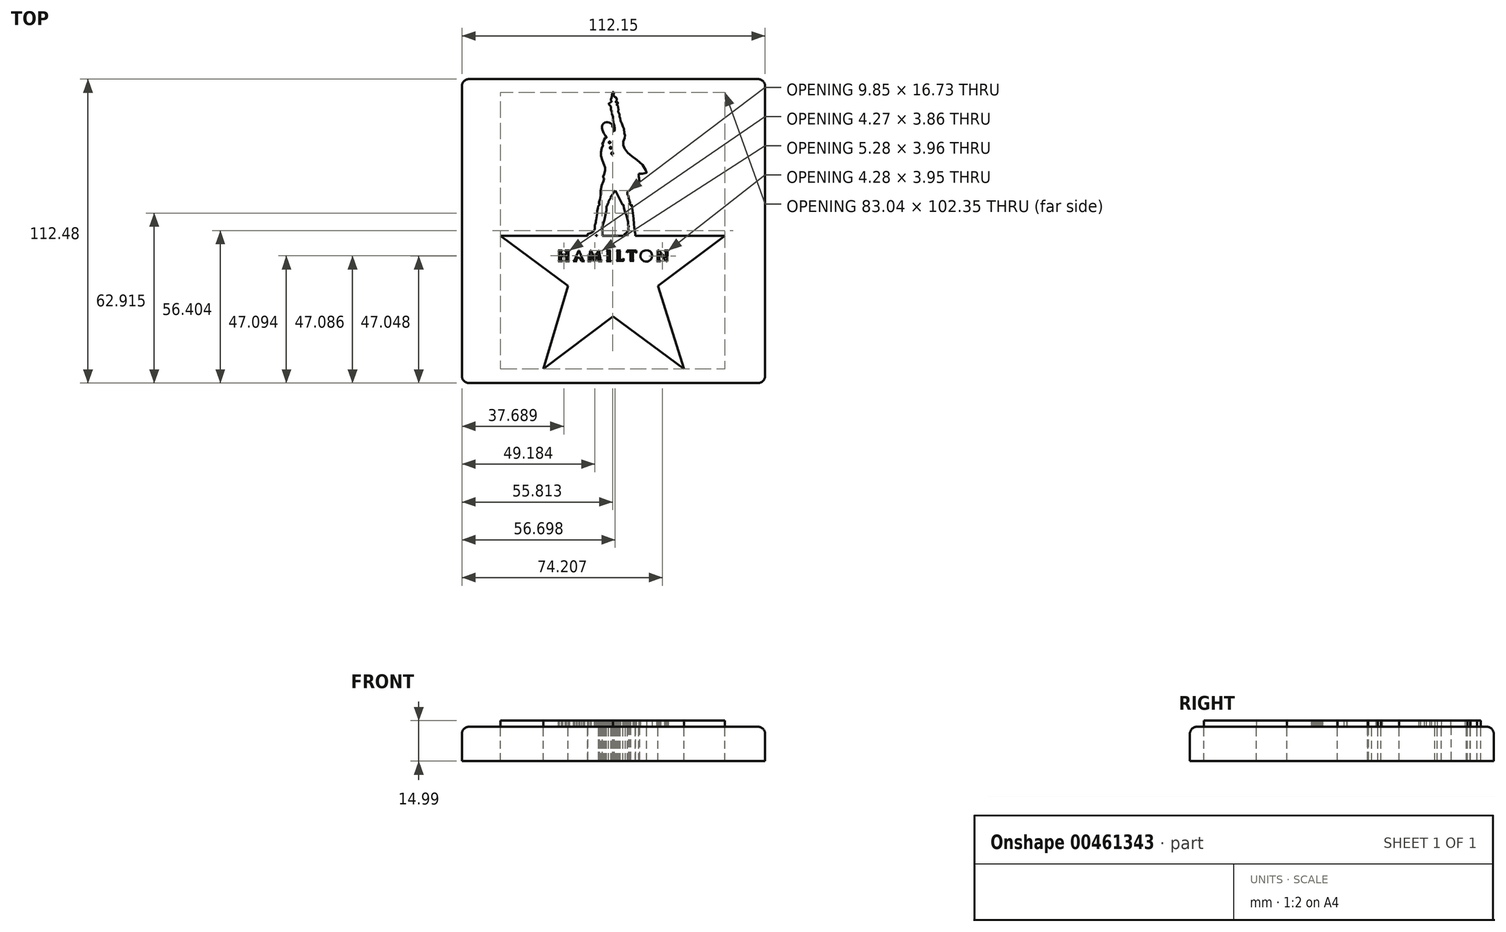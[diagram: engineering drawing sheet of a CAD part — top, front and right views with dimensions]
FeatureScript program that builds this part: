
annotation { "Feature Type Name" : "Feature", "Feature Type Description" : "" }
export const myFeature = defineFeature(function(context is Context, id is Id, definition is map)
    precondition{}
    {
        {
            var Q0;
            Q0=qCreatedBy(makeId("Top.planeOp"),FACE);
            var sketch = newSketch(context, id + "F0", { "sketchPlane" : qUnion([Q0])});
            skLineSegment(sketch, "E0.bottom", {"start": v(-76.02, 56.24) * mm, "end": v(36.13, 56.24) * mm});
            skLineSegment(sketch, "E0.top", {"start": v(-76.02, -56.24) * mm, "end": v(36.13, -56.24) * mm});
            skLineSegment(sketch, "E0.left", {"start": v(-76.02, 56.24) * mm, "end": v(-76.02, -56.24) * mm});
            skLineSegment(sketch, "E0.right", {"start": v(36.13, 56.24) * mm, "end": v(36.13, -56.24) * mm});
            skLineSegment(sketch, "E1", {"start": v(-61.73, -1.69) * mm, "end": v(21.31, -1.69) * mm});
            skLineSegment(sketch, "E2", {"start": v(21.31, -1.69) * mm, "end": v(-3.46, -20.29) * mm});
            skLineSegment(sketch, "E3", {"start": v(-3.46, -20.29) * mm, "end": v(6.1, -51.01) * mm});
            skLineSegment(sketch, "E4", {"start": v(6.1, -51.01) * mm, "end": v(-20.13, -31.64) * mm});
            skLineSegment(sketch, "E5", {"start": v(-20.13, -31.64) * mm, "end": v(-45.97, -51.01) * mm});
            skLineSegment(sketch, "E6", {"start": v(-45.97, -51.01) * mm, "end": v(-36.74, -20.29) * mm});
            skLineSegment(sketch, "E7", {"start": v(-36.74, -20.29) * mm, "end": v(-61.73, -1.69) * mm});
            skLineSegment(sketch, "E8", {"start": v(-40.47, -7.22) * mm, "end": v(-38.99, -7.22) * mm});
            skLineSegment(sketch, "E9", {"start": v(-38.99, -7.22) * mm, "end": v(-39.25, -7.42) * mm});
            skLineSegment(sketch, "E10", {"start": v(-39.25, -7.42) * mm, "end": v(-39.25, -8.79) * mm});
            skLineSegment(sketch, "E11", {"start": v(-39.25, -8.79) * mm, "end": v(-37.42, -8.79) * mm});
            skLineSegment(sketch, "E12", {"start": v(-40.47, -7.22) * mm, "end": v(-40.03, -7.54) * mm});
            skLineSegment(sketch, "E13", {"start": v(-40.03, -7.54) * mm, "end": v(-40.03, -10.72) * mm});
            skLineSegment(sketch, "E14", {"start": v(-40.03, -10.72) * mm, "end": v(-40.47, -11.08) * mm});
            skLineSegment(sketch, "E15", {"start": v(-40.47, -11.08) * mm, "end": v(-38.8, -11.08) * mm});
            skLineSegment(sketch, "E16", {"start": v(-39.25, -9.22) * mm, "end": v(-37.46, -9.22) * mm});
            skLineSegment(sketch, "E17", {"start": v(-37.46, -9.22) * mm, "end": v(-37.46, -10.72) * mm});
            skPoint(sketch, "E18.start.orphan", {"position": v(-39.18, -10.72) * mm});
            skLineSegment(sketch, "E19", {"start": v(-39.25, -9.22) * mm, "end": v(-39.25, -10.73) * mm});
            skLineSegment(sketch, "E20", {"start": v(-39.25, -10.73) * mm, "end": v(-38.8, -11.08) * mm});
            skLineSegment(sketch, "E21", {"start": v(-37.46, -10.72) * mm, "end": v(-37.82, -11.08) * mm});
            skLineSegment(sketch, "E22", {"start": v(-37.82, -11.08) * mm, "end": v(-36.2, -11.08) * mm});
            skLineSegment(sketch, "E23", {"start": v(-36.2, -11.08) * mm, "end": v(-36.62, -10.72) * mm});
            skLineSegment(sketch, "E24", {"start": v(-36.62, -10.72) * mm, "end": v(-36.62, -7.61) * mm});
            skPoint(sketch, "E25.end.orphan", {"position": v(-36.2, -7.32) * mm});
            skLineSegment(sketch, "E26", {"start": v(-37.42, -8.79) * mm, "end": v(-37.42, -7.54) * mm});
            skLineSegment(sketch, "E27", {"start": v(-37.42, -7.54) * mm, "end": v(-37.88, -7.22) * mm});
            skLineSegment(sketch, "E28", {"start": v(-37.88, -7.22) * mm, "end": v(-36.23, -7.22) * mm});
            skLineSegment(sketch, "E29", {"start": v(-36.23, -7.22) * mm, "end": v(-36.62, -7.61) * mm});
            skLineSegment(sketch, "E30", {"start": v(-32.93, -8.38) * mm, "end": v(-33.3, -9.34) * mm});
            skLineSegment(sketch, "E31", {"start": v(-33.3, -9.34) * mm, "end": v(-32.52, -9.34) * mm});
            skLineSegment(sketch, "E32", {"start": v(-32.52, -9.34) * mm, "end": v(-32.93, -8.38) * mm});
            skLineSegment(sketch, "E33", {"start": v(-33.5, -11.1) * mm, "end": v(-34.91, -11.1) * mm});
            skLineSegment(sketch, "E34", {"start": v(-34.91, -11.1) * mm, "end": v(-34.4, -10.75) * mm});
            skLineSegment(sketch, "E35", {"start": v(-34.4, -10.75) * mm, "end": v(-32.86, -7.19) * mm});
            skLineSegment(sketch, "E36", {"start": v(-32.86, -7.19) * mm, "end": v(-32.7, -7.19) * mm});
            skLineSegment(sketch, "E37", {"start": v(-32.7, -7.19) * mm, "end": v(-31.12, -10.83) * mm});
            skLineSegment(sketch, "E38", {"start": v(-33.5, -9.83) * mm, "end": v(-32.43, -9.83) * mm});
            skLineSegment(sketch, "E39", {"start": v(-32.43, -9.83) * mm, "end": v(-31.86, -11.1) * mm});
            skLineSegment(sketch, "E40", {"start": v(-31.86, -11.1) * mm, "end": v(-30.73, -11.1) * mm});
            skLineSegment(sketch, "E41", {"start": v(-30.73, -11.1) * mm, "end": v(-31.12, -10.83) * mm});
            skLineSegment(sketch, "E42", {"start": v(-33.5, -9.83) * mm, "end": v(-33.78, -10.76) * mm});
            skLineSegment(sketch, "E43", {"start": v(-33.78, -10.76) * mm, "end": v(-33.5, -11.1) * mm});
            skLineSegment(sketch, "E44", {"start": v(-29.48, -11.12) * mm, "end": v(-28.2, -11.12) * mm});
            skLineSegment(sketch, "E45", {"start": v(-25.57, -11.13) * mm, "end": v(-24.2, -11.13) * mm});
            skLineSegment(sketch, "E46", {"start": v(-26.96, -9.88) * mm, "end": v(-28.25, -7.22) * mm});
            skLineSegment(sketch, "E47", {"start": v(-28.25, -7.22) * mm, "end": v(-28.48, -7.22) * mm});
            skLineSegment(sketch, "E48", {"start": v(-28.48, -7.22) * mm, "end": v(-29.08, -10.74) * mm});
            skLineSegment(sketch, "E49", {"start": v(-29.08, -10.74) * mm, "end": v(-29.48, -11.12) * mm});
            skLineSegment(sketch, "E50", {"start": v(-28.25, -8.74) * mm, "end": v(-28.45, -10.82) * mm});
            skLineSegment(sketch, "E51", {"start": v(-28.45, -10.82) * mm, "end": v(-28.2, -11.12) * mm});
            skLineSegment(sketch, "E52", {"start": v(-26.96, -9.88) * mm, "end": v(-25.47, -7.16) * mm});
            skLineSegment(sketch, "E53", {"start": v(-25.47, -7.16) * mm, "end": v(-25.31, -7.16) * mm});
            skLineSegment(sketch, "E54", {"start": v(-25.31, -7.16) * mm, "end": v(-24.73, -10.71) * mm});
            skLineSegment(sketch, "E55", {"start": v(-24.73, -10.71) * mm, "end": v(-24.2, -11.13) * mm});
            skLineSegment(sketch, "E56", {"start": v(-25.57, -11.13) * mm, "end": v(-25.79, -8.65) * mm});
            skLineSegment(sketch, "E57", {"start": v(-25.79, -8.65) * mm, "end": v(-26.87, -11.13) * mm});
            skLineSegment(sketch, "E58", {"start": v(-26.87, -11.13) * mm, "end": v(-27.18, -11.13) * mm});
            skLineSegment(sketch, "E59", {"start": v(-27.18, -11.13) * mm, "end": v(-28.25, -8.74) * mm});
            skLineSegment(sketch, "E60", {"start": v(-22.52, -11.13) * mm, "end": v(-20.8, -11.13) * mm});
            skLineSegment(sketch, "E61", {"start": v(-20.8, -11.13) * mm, "end": v(-21.29, -10.76) * mm});
            skLineSegment(sketch, "E62", {"start": v(-21.29, -10.76) * mm, "end": v(-21.29, -7.64) * mm});
            skLineSegment(sketch, "E63", {"start": v(-21.29, -7.64) * mm, "end": v(-20.98, -7.25) * mm});
            skLineSegment(sketch, "E64", {"start": v(-20.98, -7.25) * mm, "end": v(-22.5, -7.25) * mm});
            skLineSegment(sketch, "E65", {"start": v(-22.5, -7.25) * mm, "end": v(-22.18, -7.51) * mm});
            skLineSegment(sketch, "E66", {"start": v(-22.18, -7.51) * mm, "end": v(-22.18, -10.69) * mm});
            skLineSegment(sketch, "E67", {"start": v(-22.18, -10.69) * mm, "end": v(-22.52, -11.13) * mm});
            skLineSegment(sketch, "E68", {"start": v(-3.55, -10.72) * mm, "end": v(-3.55, -7.22) * mm});
            skLineSegment(sketch, "E69", {"start": v(-3.55, -7.22) * mm, "end": v(-3.14, -7.22) * mm});
            skLineSegment(sketch, "E70", {"start": v(-3.14, -7.22) * mm, "end": v(-0.57, -9.94) * mm});
            skLineSegment(sketch, "E71", {"start": v(-0.57, -9.94) * mm, "end": v(-0.57, -7.56) * mm});
            skLineSegment(sketch, "E72", {"start": v(-0.57, -7.56) * mm, "end": v(-1.04, -7.24) * mm});
            skLineSegment(sketch, "E73", {"start": v(-1.04, -7.24) * mm, "end": v(0.33, -7.24) * mm});
            skLineSegment(sketch, "E74", {"start": v(0.33, -7.24) * mm, "end": v(0, -7.59) * mm});
            skLineSegment(sketch, "E75", {"start": v(0, -7.59) * mm, "end": v(-0.07, -11.15) * mm});
            skLineSegment(sketch, "E76", {"start": v(-3.57, -10.77) * mm, "end": v(-3.95, -11.1) * mm});
            skLineSegment(sketch, "E77", {"start": v(-3.95, -11.1) * mm, "end": v(-2.47, -11.1) * mm});
            skLineSegment(sketch, "E78", {"start": v(-3.01, -8.39) * mm, "end": v(-3.01, -10.73) * mm});
            skLineSegment(sketch, "E79", {"start": v(-2.98, -10.78) * mm, "end": v(-2.47, -11.1) * mm});
            skPoint(sketch, "E80.visualSharp", {"position": v(-3.01, -10.76) * mm});
            skArc(sketch, "E80.filletArc", {"start": v(-3.01, -10.73) * mm, "mid": v(-3, -10.76) * mm, "end": v(-2.98, -10.78) * mm});
            skPoint(sketch, "E81.visualSharp", {"position": v(-3.55, -10.75) * mm});
            skArc(sketch, "E81.filletArc", {"start": v(-3.57, -10.77) * mm, "mid": v(-3.56, -10.75) * mm, "end": v(-3.55, -10.72) * mm});
            skLineSegment(sketch, "E82", {"start": v(-3.01, -8.39) * mm, "end": v(-0.4, -11.17) * mm});
            skLineSegment(sketch, "E83", {"start": v(-0.4, -11.17) * mm, "end": v(-0.07, -11.15) * mm});
            skFitSpline(sketch, "E84", {"points": [v(-9.92, -9.5) * mm, v(-9.9, -8.45) * mm, v(-8.8, -7.33) * mm, v(-7.1, -7.17) * mm, v(-6.68, -7.33) * mm, v(-5.96, -7.91) * mm, v(-5.7, -9.37) * mm, v(-6.11, -10.46) * mm, v(-7.1, -11.19) * mm, v(-8.73, -11.1) * mm, v(-9.63, -10.29) * mm, v(-9.92, -9.5) * mm]});
            skFitSpline(sketch, "E85", {"points": [v(-8.98, -8.18) * mm, v(-8.34, -7.58) * mm, v(-7.6, -7.53) * mm, v(-6.95, -7.94) * mm, v(-6.56, -8.78) * mm, v(-6.57, -9.86) * mm, v(-6.8, -10.35) * mm, v(-7.14, -10.7) * mm, v(-8.22, -10.7) * mm, v(-8.94, -9.95) * mm, v(-8.98, -8.18) * mm]});
            skFitSpline(sketch, "E86", {"points": [v(-8.94, -9.95) * mm, v(-9.06, -9.71) * mm, v(-9.08, -8.45) * mm, v(-8.98, -8.18) * mm], "startDerivative": vector(-0.58, 0.64) * mm, "endDerivative": vector(0.46, 0.75) * mm});
            skPoint(sketch, "E87", {"position": v(-8.9, -10.05) * mm});
            skFitSpline(sketch, "E88", {"points": [v(-8.9, -10.05) * mm, v(-9.02, -9.9) * mm, v(-9.06, -9.71) * mm], "startDerivative": vector(-0.27, 0.3) * mm, "endDerivative": vector(-0.06, 0.38) * mm});
            skLineSegment(sketch, "E89", {"start": v(-18.83, -7.22) * mm, "end": v(-17.28, -7.22) * mm});
            skLineSegment(sketch, "E90", {"start": v(-18.83, -7.22) * mm, "end": v(-18.51, -7.43) * mm});
            skLineSegment(sketch, "E91", {"start": v(-18.51, -7.43) * mm, "end": v(-18.51, -10.7) * mm});
            skLineSegment(sketch, "E92", {"start": v(-18.51, -10.7) * mm, "end": v(-18.83, -11.05) * mm});
            skLineSegment(sketch, "E93", {"start": v(-18.83, -11.05) * mm, "end": v(-16.42, -11.05) * mm});
            skLineSegment(sketch, "E94", {"start": v(-17.28, -7.22) * mm, "end": v(-17.62, -7.44) * mm});
            skLineSegment(sketch, "E95", {"start": v(-17.62, -7.44) * mm, "end": v(-17.62, -10.4) * mm});
            skLineSegment(sketch, "E96", {"start": v(-14.9, -7.2) * mm, "end": v(-11.53, -7.2) * mm});
            skLineSegment(sketch, "E97", {"start": v(-11.53, -7.2) * mm, "end": v(-11.53, -8.05) * mm});
            skLineSegment(sketch, "E98", {"start": v(-14.9, -7.2) * mm, "end": v(-15.08, -7.92) * mm});
            skLineSegment(sketch, "E99", {"start": v(-15.08, -7.92) * mm, "end": v(-14.64, -7.6) * mm});
            skLineSegment(sketch, "E100", {"start": v(-14.64, -7.6) * mm, "end": v(-13.65, -7.6) * mm});
            skLineSegment(sketch, "E101", {"start": v(-13.65, -7.6) * mm, "end": v(-13.65, -10.8) * mm});
            skLineSegment(sketch, "E102", {"start": v(-13.65, -10.8) * mm, "end": v(-13.95, -11.03) * mm});
            skLineSegment(sketch, "E103", {"start": v(-13.95, -11.03) * mm, "end": v(-12.36, -11.03) * mm});
            skLineSegment(sketch, "E104", {"start": v(-12.36, -11.03) * mm, "end": v(-12.76, -10.83) * mm});
            skLineSegment(sketch, "E105", {"start": v(-12.76, -10.83) * mm, "end": v(-12.76, -7.6) * mm});
            skLineSegment(sketch, "E106", {"start": v(-12.76, -7.6) * mm, "end": v(-12, -7.6) * mm});
            skFitSpline(sketch, "E107", {"points": [v(-16.42, -11.05) * mm, v(-16.26, -11) * mm, v(-16.16, -10.71) * mm, v(-16.2, -10.12) * mm], "startDerivative": vector(0.72, 0.1) * mm, "endDerivative": vector(-0.15, 1.4) * mm});
            skFitSpline(sketch, "E108", {"points": [v(-16.2, -10.12) * mm, v(-16.51, -10.56) * mm, v(-16.76, -10.67) * mm, v(-17.6, -10.67) * mm], "startDerivative": vector(-0.98, -1.52) * mm, "endDerivative": vector(-2.32, 0.08) * mm});
            skLineSegment(sketch, "E109", {"start": v(-17.62, -10.4) * mm, "end": v(-17.6, -10.62) * mm});
            skArc(sketch, "E110.filletArc", {"start": v(-17.6, -10.62) * mm, "mid": v(-17.6, -10.66) * mm, "end": v(-17.56, -10.68) * mm});
            skFitSpline(sketch, "E111", {"points": [v(-11.53, -8.05) * mm, v(-11.58, -7.97) * mm, v(-11.7, -7.76) * mm, v(-11.88, -7.61) * mm, v(-12, -7.6) * mm], "startDerivative": vector(-0.25, 0.35) * mm, "endDerivative": vector(-0.54, -0.01) * mm});
            skFitSpline(sketch, "E112", {"points": [v(-11.7, -7.76) * mm, v(-11.65, -7.82) * mm, v(-11.57, -7.95) * mm, v(-11.53, -8.05) * mm], "startDerivative": vector(0.2, -0.2) * mm, "endDerivative": vector(0.12, -0.3) * mm});
            skCircle(sketch, "E113", {"center": v(-21.4, 32.82) * mm, "radius": 0.32 * mm});
            skCircle(sketch, "E114", {"center": v(-20.99, 30.86) * mm, "radius": 0.35 * mm});
            skCircle(sketch, "E115", {"center": v(-20.44, 28.78) * mm, "radius": 0.37 * mm});
            skFitSpline(sketch, "E116", {"points": [v(-10.62, 21.23) * mm, v(-9.35, 21.26) * mm, v(-7.76, 21.58) * mm, v(-7.74, 21.9) * mm, v(-8.5, 23.58) * mm, v(-11.67, 26.66) * mm, v(-14.06, 28.42) * mm, v(-15.63, 30.25) * mm, v(-16.21, 31.52) * mm, v(-16.4, 32.35) * mm, v(-16, 34.28) * mm, v(-15.63, 34.7) * mm, v(-15.65, 35.55) * mm, v(-15.87, 36.01) * mm, v(-16.04, 36.45) * mm, v(-16.11, 38.14) * mm, v(-16.3, 38.53) * mm, v(-16.7, 39) * mm, v(-16.85, 40.19) * mm, v(-17.24, 40.72) * mm, v(-17.5, 41.12) * mm, v(-17.48, 42.04) * mm, v(-17.65, 42.19) * mm, v(-17.76, 42.34) * mm, v(-17.64, 42.82) * mm, v(-17.81, 43.5) * mm, v(-18.25, 44.15) * mm, v(-18.27, 44.48) * mm, v(-18.14, 44.97) * mm, v(-18.35, 46.51) * mm], "startDerivative": vector(28.18, -0.5) * mm, "endDerivative": vector(-8.2, 39.94) * mm});
            skFitSpline(sketch, "E117", {"points": [v(-18.35, 46.51) * mm, v(-18.78, 46.73) * mm, v(-18.35, 47.24) * mm, v(-18.35, 47.59) * mm, v(-18.96, 47.59) * mm, v(-19.03, 47.96) * mm, v(-18.85, 48.2) * mm, v(-18.85, 49.33) * mm, v(-19.1, 49.49) * mm, v(-19.73, 49.9) * mm, v(-19.77, 50.04) * mm, v(-20.05, 50.03) * mm, v(-19.8, 51.1) * mm, v(-19.8, 51.4) * mm, v(-20, 51.5) * mm, v(-20.22, 51.39) * mm, v(-20.45, 50.68) * mm, v(-20.51, 49.88) * mm, v(-20.78, 49.18) * mm, v(-20.9, 48.7) * mm, v(-20.84, 48.3) * mm, v(-20.67, 48.13) * mm, v(-20.67, 47.83) * mm, v(-21.7, 47.23) * mm, v(-21.59, 46.82) * mm, v(-20.87, 46.14) * mm, v(-20.93, 45.6) * mm], "startDerivative": vector(-17.4, 4.44) * mm, "endDerivative": vector(-5.38, -13.95) * mm});
            skFitSpline(sketch, "E118", {"points": [v(-20.87, 46.14) * mm, v(-20.86, 44.7) * mm, v(-20.63, 44.45) * mm, v(-20.5, 43.3) * mm, v(-20.17, 42.52) * mm, v(-20.16, 41.16) * mm, v(-20, 40.33) * mm, v(-19.77, 39.38) * mm, v(-19.53, 38.5) * mm, v(-19.53, 37.5) * mm, v(-19.81, 36.85) * mm], "startDerivative": vector(-1.44, -14.6) * mm, "endDerivative": vector(-3.94, -6.8) * mm});
            skFitSpline(sketch, "E119", {"points": [v(-10.62, 21.23) * mm, v(-10.52, 19.75) * mm, v(-10.4, 18.22) * mm, v(-10.95, 17.4) * mm, v(-14.76, 14.5) * mm], "startDerivative": vector(0.2, -6.63) * mm, "endDerivative": vector(-11.9, -8.7) * mm});
            skFitSpline(sketch, "E120", {"points": [v(-14.76, 14.5) * mm, v(-14.76, 13.35) * mm], "startDerivative": vector(0, -1.15) * mm, "endDerivative": vector(0, -1.15) * mm});
            skFitSpline(sketch, "E121", {"points": [v(-14.76, 13.35) * mm, v(-14.5, 13.2) * mm, v(-14.32, 12.6) * mm, v(-14.4, 12.1) * mm, v(-14.11, 11.62) * mm, v(-14.01, 11.09) * mm, v(-13.94, 10.77) * mm, v(-13.7, 10.62) * mm, v(-13.88, 10.36) * mm, v(-13.93, 10.2) * mm, v(-13.57, 9.61) * mm, v(-13.33, 9.78) * mm, v(-13.1, 9.3) * mm, v(-12.22, 0.98) * mm, v(-12.12, 0.23) * mm, v(-11.95, -0.28) * mm, v(-11.92, -1.69) * mm], "startDerivative": vector(6.62, -2.15) * mm, "endDerivative": vector(-0.79, -17.8) * mm});
            skFitSpline(sketch, "E122", {"points": [v(-11.92, -1.69) * mm, v(-16, -1.69) * mm], "startDerivative": vector(-4.07, 0) * mm, "endDerivative": vector(-4.07, 0) * mm});
            skFitSpline(sketch, "E123", {"points": [v(-16, -1.69) * mm, v(-16, -1.38) * mm, v(-14.76, -0.22) * mm, v(-14.42, 0.28) * mm, v(-14.52, 1.3) * mm, v(-14.35, 1.63) * mm, v(-14.37, 1.99) * mm, v(-14.52, 1.96) * mm, v(-14.49, 2.89) * mm, v(-16.28, 9.59) * mm, v(-16.24, 9.76) * mm, v(-16.61, 9.75) * mm, v(-19.22, 14.89) * mm], "startDerivative": vector(-2.21, 5.9) * mm, "endDerivative": vector(-14.62, 37.56) * mm});
            skLineSegment(sketch, "E124", {"start": v(-16.61, 9.75) * mm, "end": v(-19.26, 15.04) * mm});
            skLineSegment(sketch, "E125", {"start": v(-19.26, 15.04) * mm, "end": v(-21.12, 12.52) * mm});
            skFitSpline(sketch, "E126", {"points": [v(-21.12, 12.52) * mm, v(-21.12, 12.1) * mm, v(-21.82, 10.95) * mm, v(-21.8, 10.5) * mm, v(-22.18, 9.84) * mm, v(-22.18, 9.5) * mm, v(-22.5, 9.18) * mm, v(-22.55, 8.07) * mm, v(-24.15, 1.7) * mm, v(-24.33, 1.36) * mm, v(-24.05, 0.82) * mm], "startDerivative": vector(1.67, -5.41) * mm, "endDerivative": vector(5.08, -7.78) * mm});
            skLineSegment(sketch, "E127", {"start": v(-24.05, 0.82) * mm, "end": v(-24.05, -1.69) * mm});
            skLineSegment(sketch, "E128", {"start": v(-24.05, -1.69) * mm, "end": v(-26.03, -1.69) * mm});
            skFitSpline(sketch, "E129", {"points": [v(-29.47, -1.69) * mm, v(-29.47, -1.06) * mm, v(-28.52, -0.8) * mm, v(-27.03, 0.38) * mm, v(-26.84, 1.91) * mm, v(-26.61, 2.83) * mm, v(-26.35, 4.34) * mm, v(-25.62, 9.43) * mm], "startDerivative": vector(-1.83, 8.4) * mm, "endDerivative": vector(3.27, 22.72) * mm});
            skFitSpline(sketch, "E130", {"points": [v(-22.95, 35.26) * mm, v(-22.58, 34.77) * mm, v(-22.58, 34.4) * mm, v(-23.01, 34.42) * mm, v(-23.42, 34.07) * mm, v(-23.46, 33.19) * mm, v(-24, 32.74) * mm, v(-24.06, 32.22) * mm, v(-23.85, 31.98) * mm, v(-24.14, 31.16) * mm, v(-24.55, 29.27) * mm, v(-24.47, 27.5) * mm, v(-23.48, 24.62) * mm, v(-23.05, 23.54) * mm, v(-23.05, 22.4) * mm, v(-23.65, 20.56) * mm, v(-23.8, 20.09) * mm, v(-23.46, 19.53) * mm, v(-23.57, 18.77) * mm, v(-24.37, 16.76) * mm, v(-24.66, 13.31) * mm, v(-24.65, 12.7) * mm, v(-25.03, 12.15) * mm, v(-24.95, 11.44) * mm, v(-25.25, 11) * mm, v(-25.16, 9.68) * mm, v(-25.62, 9.43) * mm], "startDerivative": vector(14.37, -14.76) * mm, "endDerivative": vector(-21.3, -3.62) * mm});
            skFitSpline(sketch, "E131", {"points": [v(-25.25, 11) * mm, v(-25.4, 10.67) * mm, v(-25.16, 9.68) * mm, v(-25.62, 9.43) * mm], "startDerivative": vector(-1, -1) * mm, "endDerivative": vector(-2.06, -0.42) * mm});
            skFitSpline(sketch, "E132", {"points": [v(-22.95, 35.26) * mm, v(-20.56, 39.5) * mm], "startDerivative": vector(-3.3, 5.84) * mm, "endDerivative": vector(6.79, -5.27) * mm});
            skPoint(sketch, "E133.1.internal.orphan", {"position": v(-19.81, 37.05) * mm});
            skFitSpline(sketch, "E134", {"points": [v(-22.95, 35.26) * mm, v(-23.52, 36.2) * mm, v(-24.1, 37.77) * mm, v(-24.1, 39.1) * mm, v(-23.36, 40.05) * mm, v(-22.05, 40.34) * mm, v(-21.1, 39.95) * mm, v(-20.38, 39.37) * mm, v(-20.33, 38.88) * mm, v(-20.2, 38.37) * mm, v(-19.9, 38.16) * mm, v(-19.77, 37.45) * mm, v(-19.95, 37.34) * mm, v(-19.95, 36.97) * mm, v(-19.81, 36.85) * mm], "startDerivative": vector(-6.62, 9.9) * mm, "endDerivative": vector(4.51, -1.93) * mm});
            skLineSegment(sketch, "E135", {"start": v(-29.47, -1.69) * mm, "end": v(-26.54, -1.69) * mm});
            skLineSegment(sketch, "E136", {"start": v(-26.54, -1.69) * mm, "end": v(-26.53, -1.44) * mm});
            skLineSegment(sketch, "E137", {"start": v(-26.53, -1.44) * mm, "end": v(-26.13, -1.46) * mm});
            skLineSegment(sketch, "E138", {"start": v(-26.13, -1.46) * mm, "end": v(-26.03, -1.69) * mm});
            skSolve(sketch);
        }
        {
            var Q0;
            Q0 = qSketchRegion(id + "F0", true);
            extrude(context, id + "F1", {"entities" : qUnion([Q0]), "oppositeDirection" : true, "depth" : 12.7 * mm});
        }
        {
            var Q0;
            Q0=makeQuery(id+"F1.opExtrude","CAP_EDGE",EDGE,{"disambiguationData":[OSD([sQuery(id+"F0.wireOp",EDGE,"E0.left")])],"isStart":true});
            var Q1;
            Q1=makeQuery(id+"F1.opExtrude","CAP_EDGE",EDGE,{"disambiguationData":[OSD([sQuery(id+"F0.wireOp",EDGE,"E0.top")])],"isStart":true});
            var Q2;
            Q2=makeQuery(id+"F1.opExtrude","CAP_EDGE",EDGE,{"disambiguationData":[OSD([sQuery(id+"F0.wireOp",EDGE,"E0.right")])],"isStart":true});
            var Q3;
            Q3=makeQuery(id+"F1.opExtrude","CAP_EDGE",EDGE,{"disambiguationData":[OSD([sQuery(id+"F0.wireOp",EDGE,"E0.bottom")])],"isStart":true});
            var Q4;
            Q4=makeQuery(id+"F1.opExtrude","SWEPT_EDGE",EDGE,{"disambiguationData":[OSD([sQuery(id+"F0.wireOp",EDGE,"E0.bottom"),sQuery(id+"F0.wireOp",EDGE,"E0.left")])]});
            var Q5;
            Q5=makeQuery(id+"F1.opExtrude","SWEPT_EDGE",EDGE,{"disambiguationData":[OSD([sQuery(id+"F0.wireOp",EDGE,"E0.top"),sQuery(id+"F0.wireOp",EDGE,"E0.right")])]});
            var Q6;
            Q6=makeQuery(id+"F1.opExtrude","SWEPT_EDGE",EDGE,{"disambiguationData":[OSD([sQuery(id+"F0.wireOp",EDGE,"E0.bottom"),sQuery(id+"F0.wireOp",EDGE,"E0.right")])]});
            var Q7;
            Q7=makeQuery(id+"F1.opExtrude","SWEPT_EDGE",EDGE,{"disambiguationData":[OSD([sQuery(id+"F0.wireOp",EDGE,"E0.top"),sQuery(id+"F0.wireOp",EDGE,"E0.left")])]});
            fillet(context, id + "F2", {"entities" : qUnion([Q0, Q1, Q2, Q3, Q4, Q5, Q6, Q7]), "radius" : 2.54 * mm, "tangentPropagation" : true, "allowEdgeOverflow" : false});
        }
        {
            var Q0;
            {var subQ0=sQuery(id+"F0.wireOp",EDGE,"E2");Q0=makeQuery(id+"F0.imprint","IMPRINT",FACE,{"disambiguationData":[TD([[makeQuery(id+"F0.imprint","IMPRINT",EDGE,{"derivedFrom":subQ0}),-1.0]])]});}
            var Q1;
            Q1=makeQuery(id+"F0.imprint","IMPRINT",FACE,{"disambiguationData":[TD([[makeQuery(id+"F0.imprint","IMPRINT",EDGE,{"derivedFrom":sQuery(id+"F0.wireOp",EDGE,"E113")}),-1.0]])]});
            extrude(context, id + "F3", {"entities" : qUnion([Q0, Q1]), "depth" : 2.3 * mm});
        }
    });
